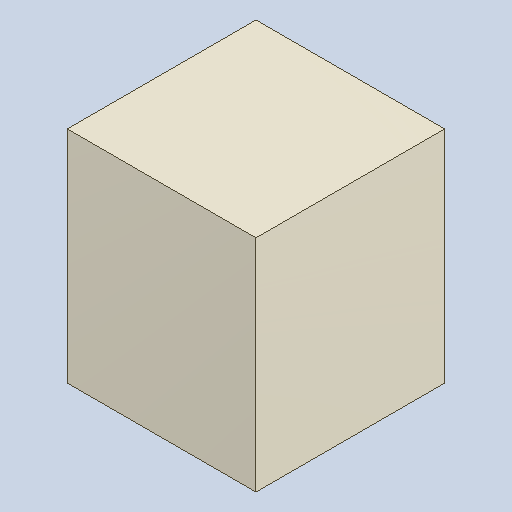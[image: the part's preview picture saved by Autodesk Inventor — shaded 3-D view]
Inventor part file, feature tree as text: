
AUTODESK INVENTOR PART (.ipt)
format: ipt  version: 2023.4 (Build 274418000, 418)  size: 82,944 bytes
history: native  units: mm
features: extrude x1
ambient origin geometry x8: Origin, YZ Plane, XZ Plane, XY Plane, X Axis, Y Axis, Z Axis, Center Point
bodies: Solid1 (feature_tree)
feature tree (1):
  extrude  "Extruded_9"  [1 undecoded]
note: 1 required parameter value undecoded (feature->parameter linkage not recoverable at this tier; creation-order binding heuristic only, values carry confidence <= 0.55)
